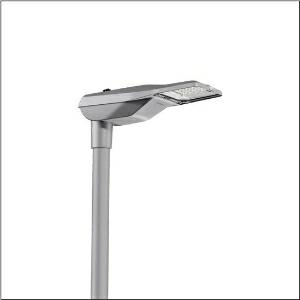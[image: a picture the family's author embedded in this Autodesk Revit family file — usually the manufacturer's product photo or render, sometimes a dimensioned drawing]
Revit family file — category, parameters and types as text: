
# Revit family: streetlight_sl_21_micro___st0_8a_5xe1c33s08db_f35f
name_source: partatom
category: Lighting Fixtures
units: mm (PartAtom-declared; Revit-internal decimal feet)

## family parameters
Cut with Voids When Loaded = No
Host = Face
Light Source = No
Part Type = Normal
Room Calculation Point = No
Round Connector Dimension = Use Diameter
Shared = No

## types (1)
- --- (1 x LED, 5110 lm, 39.1 W, 3000K)
    Apparent Load = 39 VA
    CIE Flux Codes = 38 75 97 100 100
    Color Rendering = 70
    Color Temperature = 3000K
    Default Elevation = 1800 mm
    Description = Streetlight SL 21 micro, mast luminaire, primary light control with lens, of PMMA, primary optical cover: cover, of toughened safety glass, transparent, light distribution: ST0.8a, light emission: direct distribution, primary light characteristic: asymmetric, installation type: side-entry, post-top, LED, High Power LED, rated luminous flux: 5.110lm, luminous efficacy: 131lm/W, light colour: 730, colour temperature: 3000K, control gear: D4i, control: flexible luminous flux parameterisation, time-dependent luminous flux control, constant luminous flux control, overheat protection, pre-setting: logarithmic dimming characteristic, mains connection: 220..240V, AC, 50/60Hz, start of lifetime: 39W, end of service life: 41W, reduction: 18W, luminaire housing, of diecast aluminium, powder-coated, SITECO metallic grey (DB 702S), corrosivity category C5 high according to DIN EN ISO 12944, please order mast flange separately, inclination adjustable: 0°, 5°, 10°, 15°, sealing non-destructively replaceable, multi-level sealing system, length: 528mm, width: 235mm, height: 110mm, mast flange for spigot size: 42mm (side-entry): 5XC10008XM4, 60/48mm (side-entry/post-top): 5XC10108XM2, 76/60mm (side-entry/post-top): 5XC10108XM1, Smart Interface above, protection rating (complete): IP66, insulation class (complete): insulation class II (safety insulation), certification: CE, ENEC, ENEC+, VDE, impact resistance: IK10, permissible operating ambient temperature for outdoor applications: -40..+50°C, standard-compliant lighting for roads and squares, packaging unit: 1 piece

Light Distribution: ST0.8a
    Height = 110 mm
    Lamp = 1 x LED
    Lamp Light Flux = 5110 lm
    Lamp Power = 39.1 W
    Lamp count = 1
    Length = 528 mm
    Luminous efficacy = 131 lm/W
    Manufacturer = Siteco
    ModVariant = No
    Model = 5XE1C33S08DB
    Number of Poles = 1
    OnlyDefault = Yes
    Power Factor = 1
    Product Name = Streetlight SL 21 micro | ST0.8a
    Product group = mast luminaire | pylon top
    ProductGroupID = 6100
    Protection Class = Protection class II
    Protection Degree = IP 66
    RLX_Detail_Level = 1
    RLX_Emergency_Light_Flux = 0 lm
    RLX_Emergency_Type = 0
    RLX_Emergency_Type_DB = No
    RlxData = <blob elided: 98297 chars, md5=2744b2c3>
    Socket = socket
    Standby Power = 0 W
    System Light Flux = 5110 lm
    System Power = 39 W
    Type Comments = factory setting: luminous flux: 100 % | dim-lin: 254 | 765 mA
    Type Image = l_1277292.jpg
    URL = http://relux.com
    VarID = @adj_153919
    Voltage = 0 V
    Weight = 0.00 kg
    Width = 235 mm

## geometry (parser evidence)
native form markers: Blend x4, Sweep x12
no freeform markers — native parametric forms only
